# Revit family: Casement_28_D_Top_Hung_Standard
name_source: partatom
category: Windows
revit_build: Autodesk Revit 2014 (Build: 20130308_1515(x64)
units: mm (PartAtom-declared; Revit-internal decimal feet)

## types (12) — shared parameters
Aluminium Thickness = 1 mm  [stored 0.00328084 ft]
Bead SG Gap = 13 mm  [stored 0.0426509 ft]
Bottom Hung = No
Casement Dimension = 28 mm  [stored 0.0918635 ft]
Custom Sash Height = 554 mm  [stored 1.81759 ft]
Default Sill Height = 800 mm  [stored 2.62467 ft]
Depth Bead = 14 mm  [stored 0.0459318 ft]
Description = Window 28mm, Type D top hung
Frame Center Offset = 14 mm  [stored 0.0459318 ft]
Height Panel 1 = 540 mm  [stored 1.77165 ft]
Height Sash = 524 mm  [stored 1.71916 ft]
Height Sash Opening = 554 mm  [stored 1.81759 ft]
Limit Fixed Pane Height Max = 1800 mm  [stored 5.90551 ft]
Limit Fixed Pane Height Min = 200 mm  [stored 0.656168 ft]
Limit Sash Height Max = 600 mm  [stored 1.9685 ft]
Limit Sash Height Min = 300 mm  [stored 0.984252 ft]
Limit Sash Width Max = 900 mm  [stored 2.95276 ft]
Limit Sash Width Min = 300 mm  [stored 0.984252 ft]
Limit Window Height Max = 2430 mm  [stored 7.97244 ft]
Limit Window Height Min = 830 mm  [stored 2.7231 ft]
Limit Window Width Max = 946 mm  [stored 3.10367 ft]
Limit Window Width Min = 346 mm
Manufacturer = Crealco
Model = Casement 28
Offset Bead SG Center Reversed = 14 mm  [stored 0.0459318 ft]
Offset Panel 3 Bead Top = 600 mm  [stored 1.9685 ft]
Offset Sash Left = 23 mm  [stored 0.0754593 ft]
Offset Sash Top = 23 mm  [stored 0.0754593 ft]
Offset Transom Top = 570 mm  [stored 1.87008 ft]
Offset Window Exterior = 14 mm  [stored 0.0459318 ft]
SG Gasket Thickness = 6 mm  [stored 0.019685 ft]
Sash Center Offset = 11 mm  [stored 0.0360892 ft]
Sash Overlap = 7 mm  [stored 0.0229659 ft]
Sash Spacing Inner = 8 mm  [stored 0.0262467 ft]
Single Glazing = Yes
Top Hung = Yes
URL = http://www.crealco.co.za
Wall Closure = By host
Width Bead = 15 mm  [stored 0.0492126 ft]
Width Profile = 30 mm  [stored 0.0984252 ft]
zero-valued in all types: Window Exterior Offset

## per-type parameters (varying)
| type | Area Pane Bottom | Area Pane Top | Clearvue SHGC Value | Clearvue U Value | Custom Windload | Custom Window Height | Custom Window Width | Energy Advantage SHGC Value | Energy Advantage U Value | Height | Height Panel 3 | Intruderprufe LowE SHGC Value | Intruderprufe LowE U Value | Intruderprufe SHGC Value | Intruderprufe U Value | Length Transom | Max Pane Area | Width | Width Panel 1 | Width Panel 3 | Width Sash | Width Sash Opening | Windload Design |
| 28-0609T-1000Pa | 0.13 m² | 0.23 m² | 0.531 | 6.19 | 1000 mm  [stored 3.28084 ft] | 890 mm  [stored 2.91995 ft] | 590 mm  [stored 1.9357 ft] | 0.492 | 4.889 | 890 mm  [stored 2.91995 ft] | 260 mm | 0.449 | 4.85 | 0.517 | 6.17 | 530 mm  [stored 1.73885 ft] | 0.23 m² | 590 mm  [stored 1.9357 ft] | 530 mm  [stored 1.73885 ft] | 530 mm  [stored 1.73885 ft] | 514 mm | 544 mm  [stored 1.78478 ft] | 1000 mm  [stored 3.28084 ft] |
| 28-0909T-1000Pa | 0.21 m² | 0.37 m² | 0.577 | 6.15 | 1000 mm  [stored 3.28084 ft] | 890 mm  [stored 2.91995 ft] | 890 mm  [stored 2.91995 ft] | 0.534 | 4.75 | 890 mm  [stored 2.91995 ft] | 260 mm | 0.486 | 4.69 | 0.561 | 6.13 | 830 mm  [stored 2.7231 ft] | 0.37 m² | 890 mm  [stored 2.91995 ft] | 830 mm  [stored 2.7231 ft] | 830 mm  [stored 2.7231 ft] | 814 mm  [stored 2.6706 ft] | 844 mm  [stored 2.76903 ft] | 1000 mm  [stored 3.28084 ft] |
| 28-0612T-1000Pa | 0.29 m² | 0.23 m² | 0.58 | 6.13 | 1000 mm  [stored 3.28084 ft] | 1190 mm  [stored 3.9042 ft] | 590 mm  [stored 1.9357 ft] | 0.531 | 4.72 | 1190 mm  [stored 3.9042 ft] | 560 mm | 0.488 | 4.66 | 0.558 | 6.09 | 530 mm  [stored 1.73885 ft] | 0.29 m² | 590 mm  [stored 1.9357 ft] | 530 mm  [stored 1.73885 ft] | 530 mm  [stored 1.73885 ft] | 514 mm | 544 mm  [stored 1.78478 ft] | 1000 mm  [stored 3.28084 ft] |
| 28-0912T-1000Pa | 0.45 m² | 0.37 m² | 0.624 | 6.1 | 1000 mm  [stored 3.28084 ft] | 1190 mm  [stored 3.9042 ft] | 890 mm  [stored 2.91995 ft] | 0.572 | 4.55 | 1190 mm  [stored 3.9042 ft] | 560 mm | 0.524 | 4.5 | 0.601 | 6.06 | 830 mm  [stored 2.7231 ft] | 0.45 m² | 890 mm  [stored 2.91995 ft] | 830 mm  [stored 2.7231 ft] | 830 mm  [stored 2.7231 ft] | 814 mm  [stored 2.6706 ft] | 844 mm  [stored 2.76903 ft] | 1000 mm  [stored 3.28084 ft] |
| 28-0609T-1500Pa | 0.13 m² | 0.23 m² | 0.531 | 6.19 | 1500 mm  [stored 4.92126 ft] | 890 mm  [stored 2.91995 ft] | 590 mm  [stored 1.9357 ft] | 0.492 | 4.889 | 890 mm  [stored 2.91995 ft] | 260 mm | 0.449 | 4.85 | 0.517 | 6.17 | 530 mm  [stored 1.73885 ft] | 0.23 m² | 590 mm  [stored 1.9357 ft] | 530 mm  [stored 1.73885 ft] | 530 mm  [stored 1.73885 ft] | 514 mm | 544 mm  [stored 1.78478 ft] | 1500 mm  [stored 4.92126 ft] |
| 28-0609T-2000Pa | 0.13 m² | 0.23 m² | 0.531 | 6.19 | 2000 mm  [stored 6.56168 ft] | 890 mm  [stored 2.91995 ft] | 590 mm  [stored 1.9357 ft] | 0.492 | 4.889 | 890 mm  [stored 2.91995 ft] | 260 mm | 0.449 | 4.85 | 0.517 | 6.17 | 530 mm  [stored 1.73885 ft] | 0.23 m² | 590 mm  [stored 1.9357 ft] | 530 mm  [stored 1.73885 ft] | 530 mm  [stored 1.73885 ft] | 514 mm | 544 mm  [stored 1.78478 ft] | 2000 mm  [stored 6.56168 ft] |
| 28-0612T-1500Pa | 0.29 m² | 0.23 m² | 0.58 | 6.13 | 1500 mm  [stored 4.92126 ft] | 1190 mm  [stored 3.9042 ft] | 590 mm  [stored 1.9357 ft] | 0.531 | 4.72 | 1190 mm  [stored 3.9042 ft] | 560 mm | 0.488 | 4.66 | 0.558 | 6.09 | 530 mm  [stored 1.73885 ft] | 0.29 m² | 590 mm  [stored 1.9357 ft] | 530 mm  [stored 1.73885 ft] | 530 mm  [stored 1.73885 ft] | 514 mm | 544 mm  [stored 1.78478 ft] | 1500 mm  [stored 4.92126 ft] |
| 28-0612T-2000Pa | 0.29 m² | 0.23 m² | 0.58 | 6.13 | 2000 mm  [stored 6.56168 ft] | 1190 mm  [stored 3.9042 ft] | 590 mm  [stored 1.9357 ft] | 0.531 | 4.72 | 1190 mm  [stored 3.9042 ft] | 560 mm | 0.488 | 4.66 | 0.558 | 6.09 | 530 mm  [stored 1.73885 ft] | 0.29 m² | 590 mm  [stored 1.9357 ft] | 530 mm  [stored 1.73885 ft] | 530 mm  [stored 1.73885 ft] | 514 mm | 544 mm  [stored 1.78478 ft] | 2000 mm  [stored 6.56168 ft] |
| 28-0909T-1500Pa | 0.21 m² | 0.37 m² | 0.577 | 6.15 | 1500 mm  [stored 4.92126 ft] | 890 mm  [stored 2.91995 ft] | 890 mm  [stored 2.91995 ft] | 0.534 | 4.75 | 890 mm  [stored 2.91995 ft] | 260 mm | 0.486 | 4.69 | 0.561 | 6.13 | 830 mm  [stored 2.7231 ft] | 0.37 m² | 890 mm  [stored 2.91995 ft] | 830 mm  [stored 2.7231 ft] | 830 mm  [stored 2.7231 ft] | 814 mm  [stored 2.6706 ft] | 844 mm  [stored 2.76903 ft] | 1500 mm  [stored 4.92126 ft] |
| 28-0909T-2000Pa | 0.21 m² | 0.37 m² | 0.577 | 6.15 | 2000 mm  [stored 6.56168 ft] | 890 mm  [stored 2.91995 ft] | 890 mm  [stored 2.91995 ft] | 0.534 | 4.75 | 890 mm  [stored 2.91995 ft] | 260 mm | 0.486 | 4.69 | 0.561 | 6.13 | 830 mm  [stored 2.7231 ft] | 0.37 m² | 890 mm  [stored 2.91995 ft] | 830 mm  [stored 2.7231 ft] | 830 mm  [stored 2.7231 ft] | 814 mm  [stored 2.6706 ft] | 844 mm  [stored 2.76903 ft] | 2000 mm  [stored 6.56168 ft] |
| 28-0912T-1500Pa | 0.45 m² | 0.37 m² | 0.624 | 6.1 | 1500 mm  [stored 4.92126 ft] | 1190 mm  [stored 3.9042 ft] | 890 mm  [stored 2.91995 ft] | 0.572 | 4.55 | 1190 mm  [stored 3.9042 ft] | 560 mm | 0.524 | 4.5 | 0.601 | 6.06 | 830 mm  [stored 2.7231 ft] | 0.45 m² | 890 mm  [stored 2.91995 ft] | 830 mm  [stored 2.7231 ft] | 830 mm  [stored 2.7231 ft] | 814 mm  [stored 2.6706 ft] | 844 mm  [stored 2.76903 ft] | 1500 mm  [stored 4.92126 ft] |
| 28-0912T-2000Pa | 0.45 m² | 0.37 m² | 0.624 | 6.1 | 2000 mm  [stored 6.56168 ft] | 1190 mm  [stored 3.9042 ft] | 890 mm  [stored 2.91995 ft] | 0.572 | 4.55 | 1190 mm  [stored 3.9042 ft] | 560 mm | 0.524 | 4.5 | 0.601 | 6.06 | 830 mm  [stored 2.7231 ft] | 0.45 m² | 890 mm  [stored 2.91995 ft] | 830 mm  [stored 2.7231 ft] | 830 mm  [stored 2.7231 ft] | 814 mm  [stored 2.6706 ft] | 844 mm  [stored 2.76903 ft] | 2000 mm  [stored 6.56168 ft] |

note: [stored X ft] marks values corroborated as IEEE doubles in the binary element streams (Revit-internal decimal feet)

## geometry (parser evidence)
native form markers: Blend x4, Sweep x26
no freeform markers — native parametric forms only
